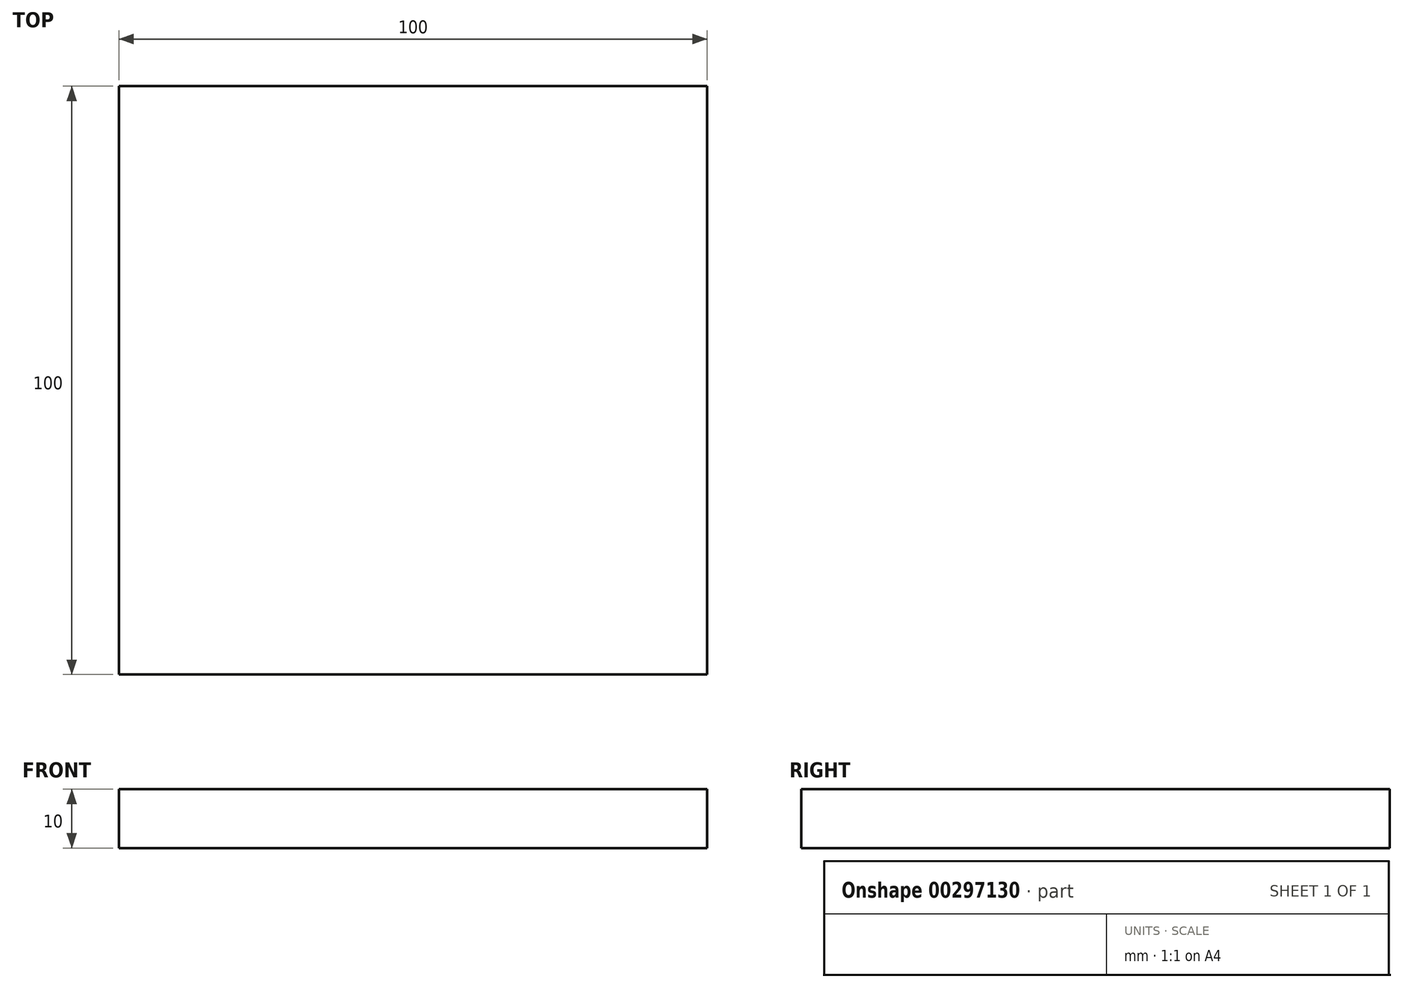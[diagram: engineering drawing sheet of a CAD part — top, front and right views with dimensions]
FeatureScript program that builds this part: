
annotation { "Feature Type Name" : "Feature", "Feature Type Description" : "" }
export const myFeature = defineFeature(function(context is Context, id is Id, definition is map)
    precondition{}
    {
        {
            var Q0;
            Q0=qCreatedBy(makeId("Top.planeOp"),FACE);
            var sketch = newSketch(context, id + "F0", { "sketchPlane" : qUnion([Q0])});
            skLineSegment(sketch, "E0.bottom", {"start": v(50, -50) * mm, "end": v(-50, -50) * mm});
            skLineSegment(sketch, "E0.top", {"start": v(50, 50) * mm, "end": v(-50, 50) * mm});
            skLineSegment(sketch, "E0.left", {"start": v(50, -50) * mm, "end": v(50, 50) * mm});
            skLineSegment(sketch, "E0.right", {"start": v(-50, -50) * mm, "end": v(-50, 50) * mm});
            skPoint(sketch, "E0.middle", {"position": v(0, 0) * mm});
            skSolve(sketch);
        }
        {
            var Q0;
            Q0=makeQuery(id+"F0.imprint","IMPRINT",FACE,{"disambiguationData":[TD([[makeQuery(id+"F0.imprint","IMPRINT",EDGE,{"derivedFrom":sQuery(id+"F0.wireOp",EDGE,"E0.bottom")}),-1.0]])]});
            extrude(context, id + "F1", {"entities" : qUnion([Q0]), "depth" : 10 * mm});
        }
    });
